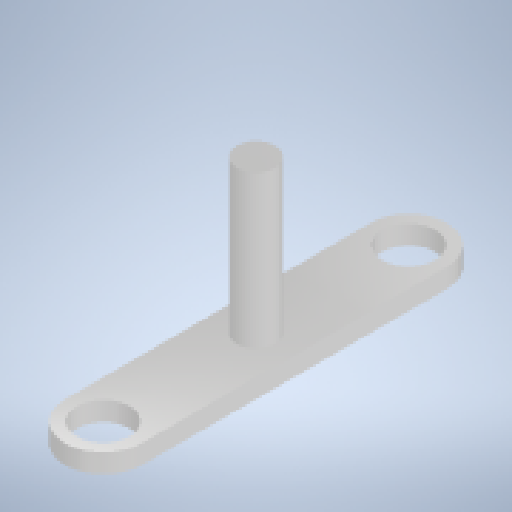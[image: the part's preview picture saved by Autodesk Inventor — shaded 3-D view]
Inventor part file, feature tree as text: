
AUTODESK INVENTOR PART (.ipt)
format: ipt  version: 2024 (Build 280153000, 153)  size: 263,680 bytes
history: native  units: in
note: dims shown in document units (in); Inventor stores cm internally (conversion verified against a paired STEP export)
features: extrude x2, sketch x2
ambient origin geometry x8: Origin, YZ Plane, XZ Plane, XY Plane, X Axis, Y Axis, Z Axis, Center Point
bodies: Body1 (feature_tree)
feature tree (4):
  extrude  "Extrusion13"  Depth=1.0in
  extrude  "Extrusion14"  Depth=2.0in
  sketch  "Sketch10"  dims[d70=0.688in d71=1.0in]
  sketch  "Sketch11"  dims[d72=4.0in d74=0.688in d75=1.0in d76=4.0in d78=0.5in d79=0.25in d80=0.0in d81=0.5in d82=2.0in d83=0.5in d84=2.0in d85=0.0in]
